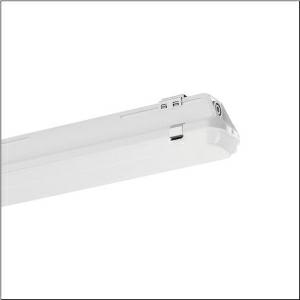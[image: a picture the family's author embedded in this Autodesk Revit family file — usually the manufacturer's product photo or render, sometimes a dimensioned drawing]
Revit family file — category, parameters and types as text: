
# Revit family: monsun_r__11_51fp10ep430l_7f44
name_source: partatom
category: Lighting Fixtures
units: mm (PartAtom-declared; Revit-internal decimal feet)

## family parameters
Cut with Voids When Loaded = No
Host = Face
Light Source = No
Part Type = Normal
Room Calculation Point = No
Round Connector Dimension = Use Diameter
Shared = No

## types (1)
- --- (1 x LED, 3840 lm, 20.5 W, 4000K)
    Apparent Load = 21 VA
    CIE Flux Codes = 47 77 93 94 100
    Color Rendering = 80
    Color Temperature = 4000K
    Default Elevation = 1800 mm
    Description = Monsun® 11, damp-proof luminaire, chain hanger, primary optical cover: enclosure, of PMMA, light emission: direct distribution, primary light characteristic: symmetric, installation type: suspended mounting, surface-mounted, horizontal mounting, vertical mounting, LED, rated luminous flux: 3.840lm, luminous efficacy: 187lm/W, light colour: 840, colour temperature: 4000K, control gear: DALI 2, with terminal, 5-pole, max. 2.5mm², mains connection: 220..240V, AC, 50/60Hz, rated input power: 21W, luminaire housing, of glass-fibre reinforced polyester, uncoated, bright grey, incl. chain hanger, length: 1.590mm, width: 90mm, height: 88mm, clip for enclosure, of stainless steel (V2A), ceiling mounting element, of stainless steel (V2A), chain hanger, of stainless steel (V2A), protection rating (complete): IP66, insulation class (complete): insulation class I (protective earthing), certification: CE, ENEC, VDE, UKCA, protection symbol: D, impact resistance: IK04, permissible operating ambient temperature: -25..+40°C, standard: EN 50419, EN 60598-2-1, corresponds to IFS (International Featured Standards) requirements for safety and quality in the food industry, for indoor or canopied outdoor use, no direct snow, no direct sun, no direct rain, LABS conformity tested according to VDMA 24364:2018-05, contact your sales advisor before using the luminaires in applications with unclear chemical exposure, large temperature fluctuations or condensation-forming humidity, packaging unit: 1 piece
    Height = 89 mm
    Lamp = 1 x LED
    Lamp Light Flux = 3840 lm
    Lamp Power = 20.5 W
    Lamp count = 1
    Length = 1590 mm
    Luminous efficacy = 187 lm/W
    Manufacturer = Siteco
    ModVariant = No
    Model = 51FP10EP430L
    Mounting Place = Ceiling
    Mounting Type = Surface mounted
    Number of Poles = 1
    OnlyDefault = Yes
    Power Factor = 1
    Product Name = Monsun® 11
    Product group = damp-proof luminaire
    ProductGroupID = 300
    Protection Class = Protection class I
    Protection Degree = IP 66
    RLX_Detail_Level = 1
    RLX_Emergency_Light_Flux = 0 lm
    RLX_Emergency_Type = 0
    RLX_Emergency_Type_DB = No
    RlxData = <blob elided: 91677 chars, md5=f8621848>
    Socket = socket
    Standby Power = 0 W
    System Light Flux = 3840 lm
    System Power = 21 W
    Type Comments = factory setting: luminous flux: 100 % | dim-lin: 254 | 136 mA
    Type Image = l_1349237.jpg
    URL = http://relux.com
    VarID = @adj_017880
    Voltage = 0 V
    Weight = 0.00 kg
    Width = 90 mm

## geometry (parser evidence)
native form markers: Blend x4, Sweep x14
no freeform markers — native parametric forms only
